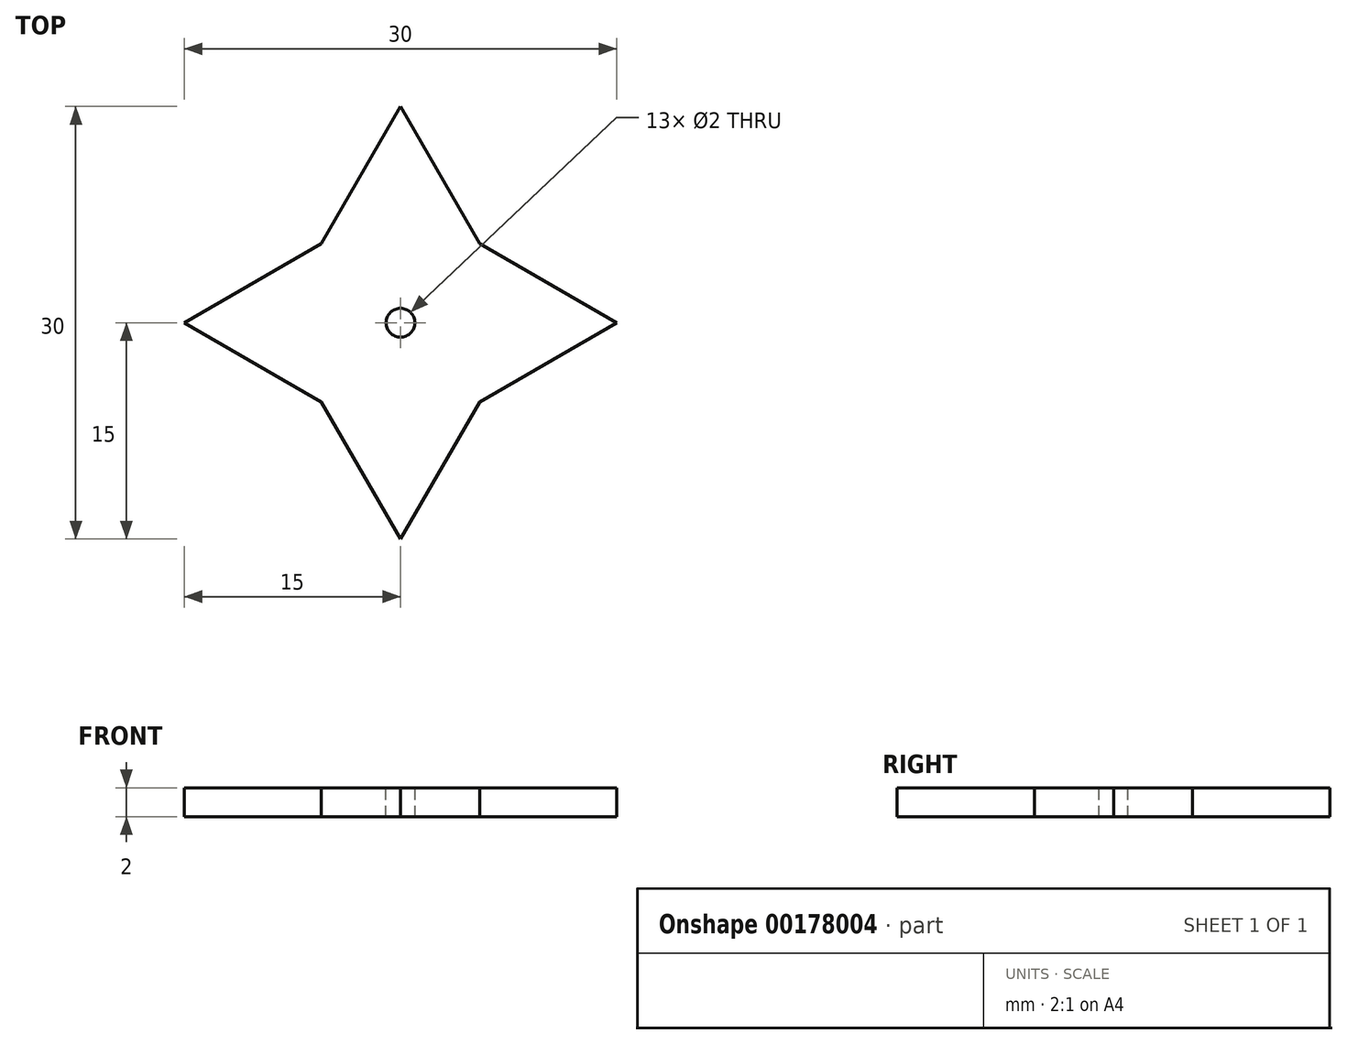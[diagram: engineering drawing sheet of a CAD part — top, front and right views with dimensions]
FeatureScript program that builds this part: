
annotation { "Feature Type Name" : "Feature", "Feature Type Description" : "" }
export const myFeature = defineFeature(function(context is Context, id is Id, definition is map)
    precondition{}
    {
        {
            var Q0;
            Q0=qCreatedBy(makeId("Top.planeOp"),FACE);
            var sketch = newSketch(context, id + "F0", { "sketchPlane" : qUnion([Q0])});
            skCircle(sketch, "E0", {"center": v(0, 0) * mm, "radius": 7.5 * mm});
            skLineSegment(sketch, "E1", {"start": v(0, 0) * mm, "end": v(0, 7.5) * mm, "construction": true});
            skLineSegment(sketch, "E2", {"start": v(0, 15) * mm, "end": v(-6.5, 3.75) * mm});
            skLineSegment(sketch, "E3.MirrorCS", {"start": v(0, 15) * mm, "end": v(6.5, 3.75) * mm});
            skLineSegment(sketch, "E4.1.0", {"start": v(-15, 0) * mm, "end": v(-3.75, -6.5) * mm});
            skLineSegment(sketch, "E4.1.1", {"start": v(-15, 0) * mm, "end": v(-3.75, 6.5) * mm});
            skLineSegment(sketch, "E4.2.0", {"start": v(0, -15) * mm, "end": v(6.5, -3.75) * mm});
            skLineSegment(sketch, "E4.2.1", {"start": v(0, -15) * mm, "end": v(-6.5, -3.75) * mm});
            skLineSegment(sketch, "E4.3.0", {"start": v(15, 0) * mm, "end": v(3.75, 6.5) * mm});
            skLineSegment(sketch, "E4.3.1", {"start": v(15, 0) * mm, "end": v(3.75, -6.5) * mm});
            skSolve(sketch);
        }
        {
            var Q0;
            Q0=qSketchRegion(id+"F0",true);
            var Q1;
            {var subQ0=sQuery(id+"F0.wireOp",EDGE,"E0");var subQ5=makeQuery(id+"F0.imprint","INTERSECT",VERTEX,{"derivedFrom":[subQ0,sQuery(id+"F0.wireOp",EDGE,"E3.MirrorCS")]});Q1=makeQuery(id+"F0.imprint","IMPRINT",FACE,{"disambiguationData":[TD([[makeQuery(id+"F0.imprint","IMPRINT",EDGE,{"disambiguationData":[TD([[subQ5,-1.0]])],"derivedFrom":subQ0}),1.0]])]});}
            extrude(context, id + "F1", {"entities" : qUnion([Q0, Q1]), "depth" : 2 * mm});
        }
        {
            var Q0;
            Q0=makeQuery(id+"F1.opExtrude","CAP_FACE",FACE,{"disambiguationData":[OSD([sQuery(id+"F0.wireOp",EDGE,"E2"),sQuery(id+"F0.wireOp",EDGE,"E3.MirrorCS"),sQuery(id+"F0.wireOp",EDGE,"E4.1.0"),sQuery(id+"F0.wireOp",EDGE,"E4.1.1"),sQuery(id+"F0.wireOp",EDGE,"E4.2.0"),sQuery(id+"F0.wireOp",EDGE,"E4.2.1"),sQuery(id+"F0.wireOp",EDGE,"E4.3.0"),sQuery(id+"F0.wireOp",EDGE,"E4.3.1")])],"isStart":false});
            var sketch = newSketch(context, id + "F2", { "sketchPlane" : qUnion([Q0])});
            skCircle(sketch, "E5", {"center": v(0, 0) * mm, "radius": 1 * mm});
            skSolve(sketch);
        }
        {
            var Q0;
            Q0 = qSketchRegion(id + "F2", true);
            extrude(context, id + "F3", {"entities" : qUnion([Q0]), "operationType" : NewBodyOperationType.REMOVE, "endBound" : BoundingType.THROUGH_ALL, "oppositeDirection" : true, "depth" : 25 * mm});
        }
    });
